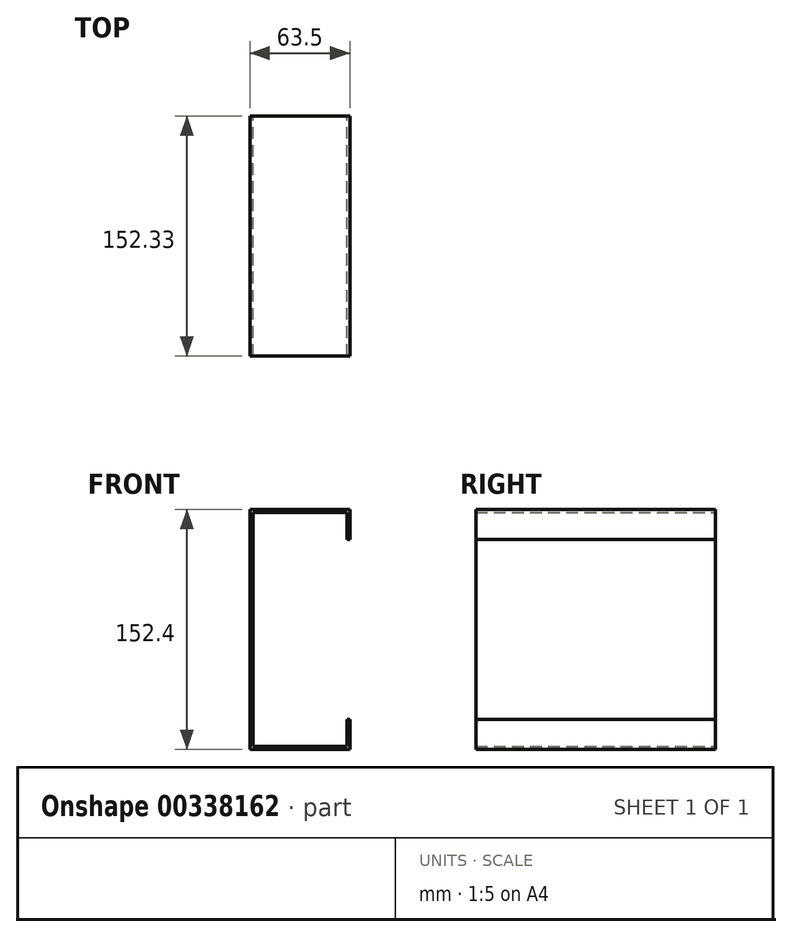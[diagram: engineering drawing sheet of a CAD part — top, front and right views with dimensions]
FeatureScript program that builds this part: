
annotation { "Feature Type Name" : "Feature", "Feature Type Description" : "" }
export const myFeature = defineFeature(function(context is Context, id is Id, definition is map)
    precondition{}
    {
        {
            var Q0;
            Q0=qCreatedBy(makeId("Front.planeOp"),FACE);
            var sketch = newSketch(context, id + "F0", { "sketchPlane" : qUnion([Q0])});
            skLineSegment(sketch, "E0.bottom", {"start": v(0, 0) * mm, "end": v(63.5, 0) * mm});
            skLineSegment(sketch, "E0.top", {"start": v(0, 152.4) * mm, "end": v(63.5, 152.4) * mm});
            skLineSegment(sketch, "E0.left", {"start": v(0, 0) * mm, "end": v(0, 152.4) * mm});
            skLineSegment(sketch, "E0.right", {"start": v(63.5, 0) * mm, "end": v(63.5, 19) * mm});
            skLineSegment(sketch, "E1.bottom", {"start": v(1.9, 1.9) * mm, "end": v(61.6, 1.9) * mm});
            skLineSegment(sketch, "E1.top", {"start": v(1.9, 150.5) * mm, "end": v(61.6, 150.5) * mm});
            skLineSegment(sketch, "E1.left", {"start": v(1.9, 1.9) * mm, "end": v(1.9, 150.5) * mm});
            skLineSegment(sketch, "E1.right", {"start": v(61.6, 1.9) * mm, "end": v(61.6, 19) * mm});
            skLineSegment(sketch, "E2", {"start": v(61.6, 19) * mm, "end": v(63.5, 19) * mm});
            skLineSegment(sketch, "E3", {"start": v(61.6, 133.4) * mm, "end": v(63.5, 133.4) * mm});
            skLineSegment(sketch, "E4.trimOffspring", {"start": v(63.5, 133.4) * mm, "end": v(63.5, 152.4) * mm});
            skLineSegment(sketch, "E5.trimOffspring", {"start": v(61.6, 133.4) * mm, "end": v(61.6, 150.5) * mm});
            skSolve(sketch);
        }
        {
            var Q0;
            Q0 = qSketchRegion(id + "F0", true);
            extrude(context, id + "F1", {"entities" : qUnion([Q0]), "depth" : 152.33 * mm});
        }
    });
